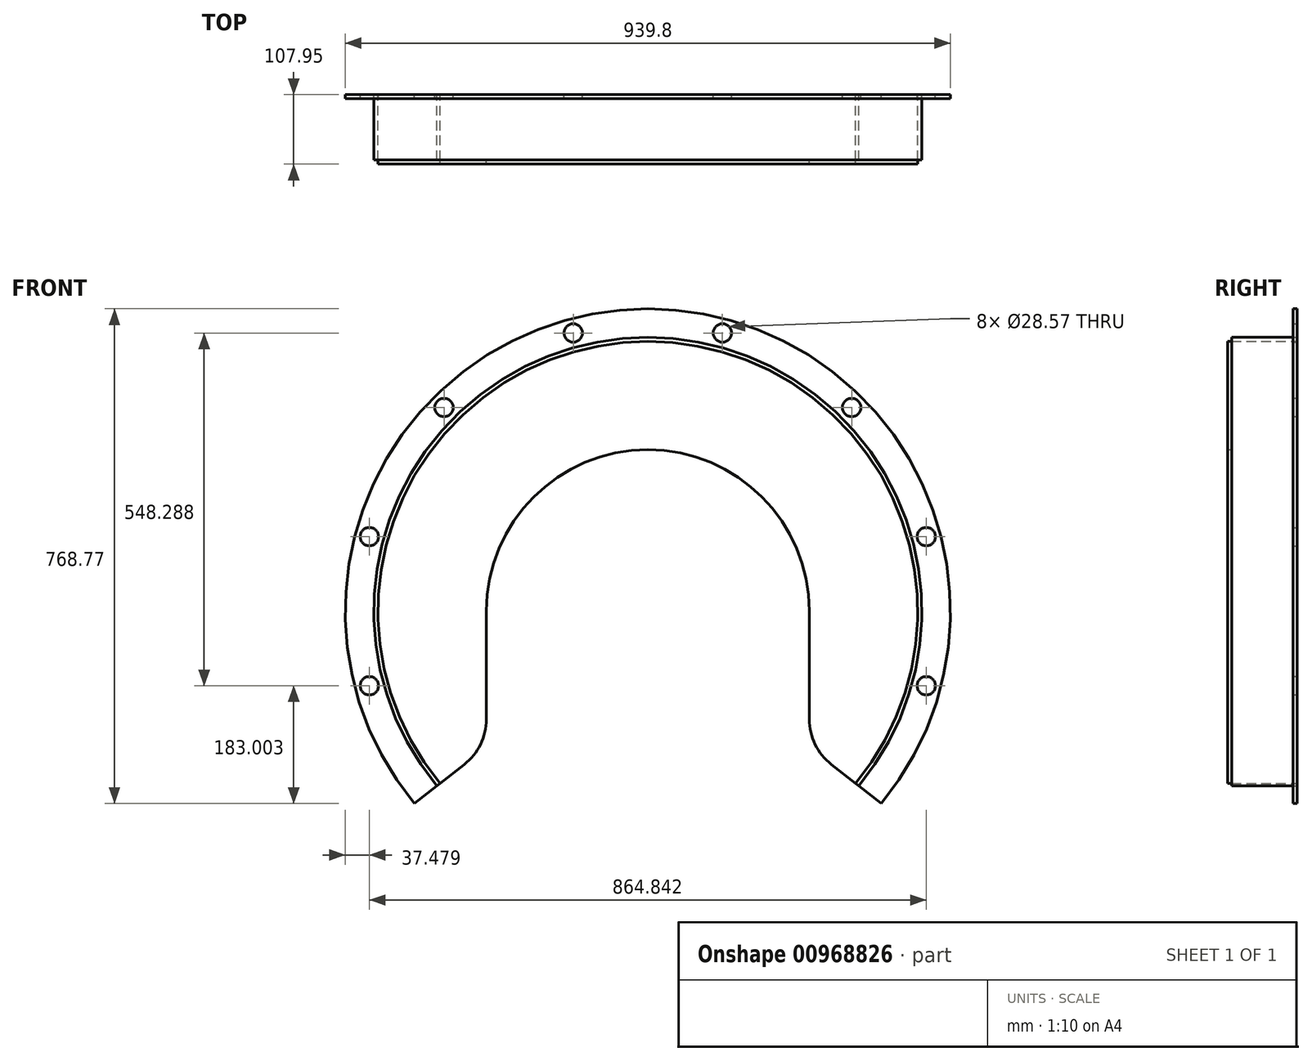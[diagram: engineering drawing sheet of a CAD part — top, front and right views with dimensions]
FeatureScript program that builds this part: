
annotation { "Feature Type Name" : "Feature", "Feature Type Description" : "" }
export const myFeature = defineFeature(function(context is Context, id is Id, definition is map)
    precondition{}
    {
        {
            var Q0;
            Q0=qCreatedBy(makeId("Front.planeOp"),FACE);
            var sketch = newSketch(context, id + "F0", { "sketchPlane" : qUnion([Q0])});
            skCircle(sketch, "E0", {"center": v(0, 0) * mm, "radius": 469.9 * mm});
            skCircle(sketch, "E1.0", {"center": v(0, 0) * mm, "radius": 425.45 * mm});
            skCircle(sketch, "E2.0", {"center": v(0, 0) * mm, "radius": 447.68 * mm, "construction": true});
            skCircle(sketch, "E3.0", {"center": v(0, 0) * mm, "radius": 419.1 * mm});
            skCircle(sketch, "E4", {"center": v(0, 0) * mm, "radius": 250.83 * mm});
            skLineSegment(sketch, "E5", {"start": v(0, 447.68) * mm, "end": v(0, 0) * mm, "construction": true});
            skLineSegment(sketch, "E6", {"start": v(0, 0) * mm, "end": v(115.87, 432.42) * mm, "construction": true});
            skPoint(sketch, "E7", {"position": v(115.87, 432.42) * mm});
            skCircle(sketch, "E8", {"center": v(115.87, 432.42) * mm, "radius": 14.29 * mm});
            skCircle(sketch, "E9.1.0", {"center": v(-115.87, 432.42) * mm, "radius": 14.29 * mm});
            skCircle(sketch, "E9.2.0", {"center": v(-316.55, 316.55) * mm, "radius": 14.29 * mm});
            skCircle(sketch, "E9.3.0", {"center": v(-432.42, 115.87) * mm, "radius": 14.29 * mm});
            skCircle(sketch, "E9.4.0", {"center": v(-432.42, -115.87) * mm, "radius": 14.29 * mm});
            skCircle(sketch, "E9.5.0", {"center": v(-316.55, -316.55) * mm, "radius": 14.29 * mm});
            skCircle(sketch, "E9.6.0", {"center": v(-115.87, -432.42) * mm, "radius": 14.29 * mm});
            skCircle(sketch, "E9.7.0", {"center": v(115.87, -432.42) * mm, "radius": 14.29 * mm});
            skCircle(sketch, "E9.8.0", {"center": v(316.55, -316.55) * mm, "radius": 14.29 * mm});
            skCircle(sketch, "E9.9.0", {"center": v(432.42, -115.87) * mm, "radius": 14.29 * mm});
            skCircle(sketch, "E9.10.0", {"center": v(432.42, 115.87) * mm, "radius": 14.29 * mm});
            skCircle(sketch, "E9.11.0", {"center": v(316.55, 316.55) * mm, "radius": 14.29 * mm});
            skPoint(sketch, "E10", {"position": v(345.1, -285.17) * mm});
            skLineSegment(sketch, "E11", {"start": v(250.83, 0) * mm, "end": v(250.83, -168.12) * mm});
            skLineSegment(sketch, "E12", {"start": v(284.96, -238.15) * mm, "end": v(362.6, -298.87) * mm});
            skPoint(sketch, "E13.newPointA", {"position": v(247.56, -208.9) * mm});
            skArc(sketch, "E13.filletArc", {"start": v(250.83, -168.12) * mm, "mid": v(259.81, -207.08) * mm, "end": v(284.96, -238.15) * mm});
            skLineSegment(sketch, "E14.MirrorCS", {"start": v(-250.83, 0) * mm, "end": v(-250.83, -168.12) * mm});
            skArc(sketch, "E15.MirrorCS", {"start": v(-250.83, -168.12) * mm, "mid": v(-259.81, -207.08) * mm, "end": v(-284.96, -238.15) * mm});
            skLineSegment(sketch, "E16.MirrorCS", {"start": v(-284.96, -238.15) * mm, "end": v(-362.6, -298.87) * mm});
            skLineSegment(sketch, "E17", {"start": v(247.56, -208.9) * mm, "end": v(247.56, -399.4) * mm, "construction": true});
            skSolve(sketch);
        }
        {
            var Q0;
            Q0=makeQuery(id+"F0.imprint","IMPRINT",FACE,{"disambiguationData":[TD([[makeQuery(id+"F0.imprint","IMPRINT",EDGE,{"derivedFrom":sQuery(id+"F0.wireOp",EDGE,"E8")}),-1.0]])]});
            extrude(context, id + "F1", {"entities" : qUnion([Q0]), "depth" : 6.35 * mm, "offsetDistance" : 25.4 * mm});
        }
        {
            var Q0;
            {var subQ0=sQuery(id+"F0.wireOp",EDGE,"E12");var subQ1=sQuery(id+"F0.wireOp",EDGE,"E1.0");var subQ2=makeQuery(id+"F0.imprint","INTERSECT",VERTEX,{"derivedFrom":[subQ1,subQ0]});Q0=makeQuery(id+"F0.imprint","IMPRINT",FACE,{"disambiguationData":[TD([[makeQuery(id+"F0.imprint","IMPRINT",EDGE,{"disambiguationData":[TD([[subQ2,-1.0]])],"derivedFrom":subQ1}),1.0]])]});}
            extrude(context, id + "F2", {"entities" : qUnion([Q0]), "depth" : 101.6 * mm, "offsetDistance" : 25.4 * mm});
        }
        {
            var Q0;
            {var subQ4=sQuery(id+"F0.wireOp",EDGE,"E11");Q0=makeQuery(id+"F0.imprint","IMPRINT",FACE,{"disambiguationData":[TD([[makeQuery(id+"F0.imprint","IMPRINT",EDGE,{"derivedFrom":subQ4}),1.0]])]});}
            extrude(context, id + "F3", {"entities" : qUnion([Q0]), "depth" : 107.95 * mm, "offsetDistance" : 25.4 * mm, "hasSecondDirection" : true, "secondDirectionOppositeDirection" : true, "secondDirectionDepth" : -101.6 * mm});
        }
    });
